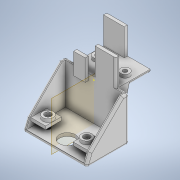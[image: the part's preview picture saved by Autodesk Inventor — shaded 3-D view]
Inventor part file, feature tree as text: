
AUTODESK INVENTOR PART (.ipt)
format: ipt  version: 2020 (Build 240168000, 168)  size: 384,000 bytes
history: native  units: in
note: dims shown in document units (in); Inventor stores cm internally (conversion verified against a paired STEP export)
features: sketch x16, extrude x15, fillet x5, plane x1, mirror x1
ambient origin geometry x8: Origin, YZ Plane, XZ Plane, XY Plane, X Axis, Y Axis, Z Axis, Center Point
bodies: Solid1 (feature_tree)
feature tree (38):
  extrude  "Extrusion1"  Depth=1.2756in
  extrude  "Extrusion3"  Depth=0.1181in
  extrude  "Extrusion4"  Depth=1.0in TaperAngle=0.0deg
  extrude  "Extrusion5"  Depth=0.1181in TaperAngle=0.0deg
  extrude  "Extrusion6"  Depth=0.1181in TaperAngle=0.0deg
  extrude  "Extrusion7"  Depth=0.3346in
  extrude  "Extrusion8"  Depth=0.1575in
  sketch  "Sketch9"  dims[d25=0.1575in d26=0.2362in d27=0.0in]
  extrude  "Extrusion9"  Depth=0.2362in TaperAngle=0.0deg
  extrude  "Extrusion10"  Depth=0.2362in
  extrude  "Extrusion11"  Depth=2.3622in
  extrude  "Extrusion12"  Depth=0.1181in
  extrude  "Extrusion13"  Depth=0.1181in
  extrude  "Extrusion14"  Depth=0.1181in
  plane  "Work Plane1"
  mirror  "Mirror1"
  extrude  "Extrusion15"  Depth=0.1181in
  extrude  "Extrusion16"  Depth=0.4331in
  fillet  "Fillet1"  Radius=0.7874in
  fillet  "Fillet2"  Radius=1.4016in
  fillet  "Fillet3"  Radius=0.1181in
  fillet  "Fillet4"  Radius=0.5906in
  fillet  "Fillet5"  Radius=0.1181in
  sketch  "Sketch1"  dims[d0=1.6142in d1=1.2756in]
  sketch  "Sketch3"  dims[d2=0.1181in d3=0.0in d8=0.1181in]
  sketch  "Sketch4"  dims[d9=0.1181in d10=1.0in d11=0.0in]
  sketch  "Sketch5"  dims[d12=0.8465in d13=0.1181in d14=0.0in]
  sketch  "Sketch6"  dims[d15=0.8465in d16=0.1181in d17=0.0in]
  sketch  "Sketch7"  dims[d20=0.3346in d21=0.3346in]
  sketch  "Sketch8"  dims[d22=0.1181in d23=0.0in d24=0.1575in]
  sketch  "Sketch10"  dims[d28=0.2362in d29=0.2362in]
  sketch  "Sketch11"  dims[d30=0.1181in d31=0.0in d32=2.3622in]
  sketch  "Sketch12"  dims[d33=0.1181in d34=0.1181in]
  sketch  "Sketch13"  dims[d35=0.1181in d36=0.1181in]
  sketch  "Sketch14"  dims[d37=1.5197in d38=0.1181in d39=0.0in d40=0.0in d41=0.1181in]
  sketch  "Sketch15"  dims[d42=0.1181in d43=0.1181in]
  sketch  "Sketch16"  dims[d44=1.4961in d45=0.0in d46=0.4331in d47=0.7874in d48=1.4016in d49=0.1181in d50=0.0in d51=0.5906in d52=0.1181in]
  sketch  "Sketch17"  dims[d53=0.5512in d54=0.0in d55=0.3937in d56=0.2362in d57=0.1181in d58=0.0in d59=0.1575in d60=0.7874in d61=0.0in d62=-1.1811in d63=0.5906in d64=0.7874in d65=0.0in d66=45.0deg d67=2.3622in d68=0.0in d69=0.0787in d70=0.0394in d71=0.0787in d72=0.0787in d73=0.0787in]
